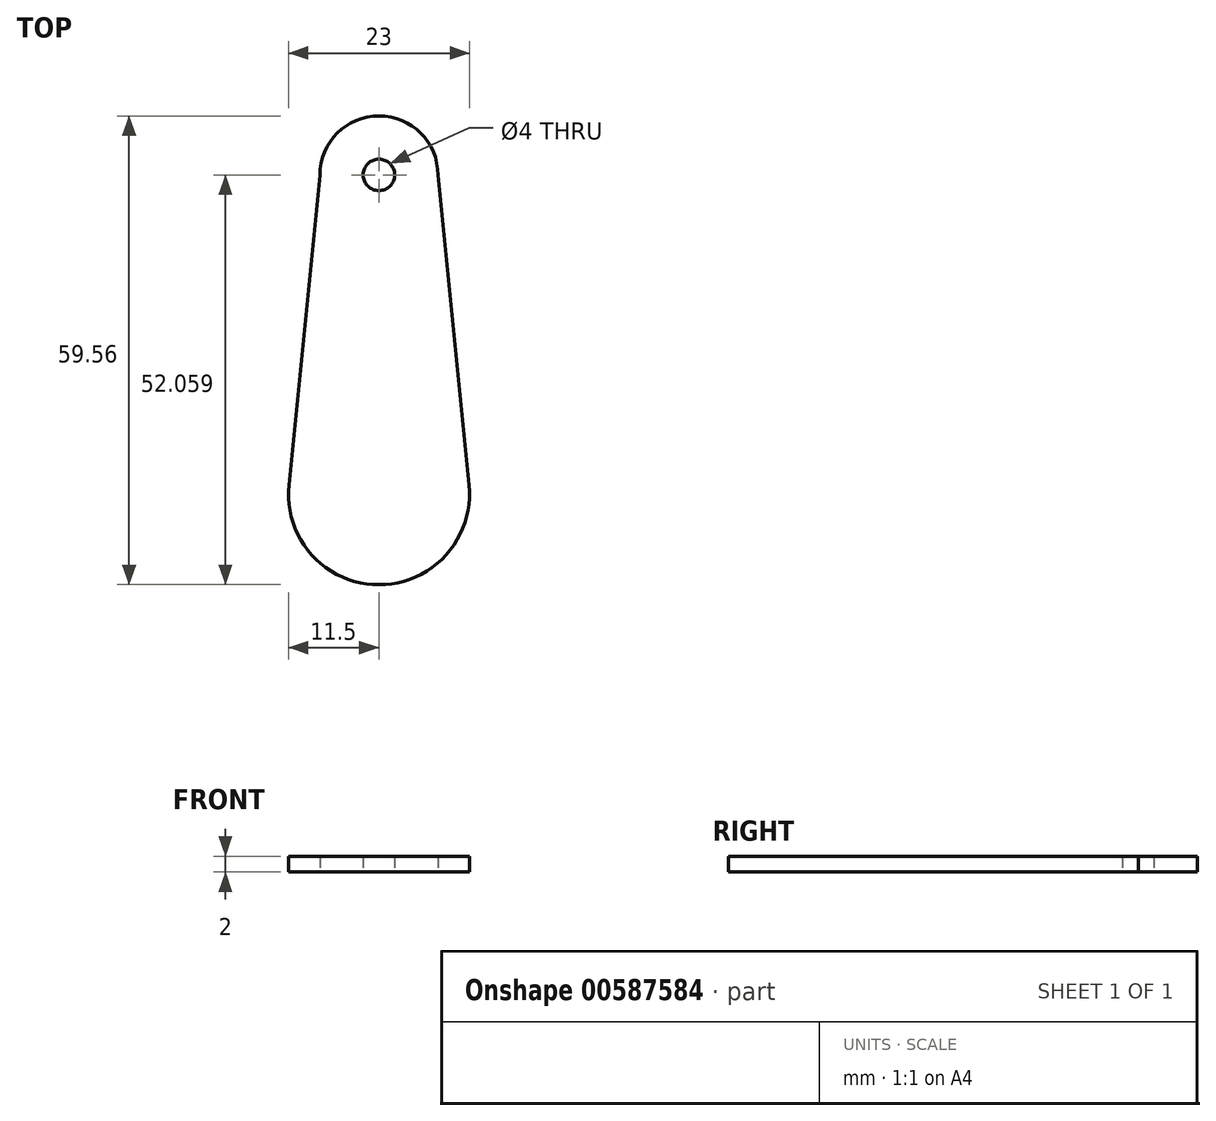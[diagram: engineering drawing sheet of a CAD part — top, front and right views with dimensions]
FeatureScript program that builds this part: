
annotation { "Feature Type Name" : "Feature", "Feature Type Description" : "" }
export const myFeature = defineFeature(function(context is Context, id is Id, definition is map)
    precondition{}
    {
        {
            var Q0;
            Q0=qCreatedBy(makeId("Top.planeOp"),FACE);
            var sketch = newSketch(context, id + "F0", { "sketchPlane" : qUnion([Q0])});
            skArc(sketch, "E0", {"start": v(-11.44, 1.14) * mm, "mid": v(0, -11.5) * mm, "end": v(11.44, 1.14) * mm});
            skArc(sketch, "E1", {"start": v(7.5, 40.56) * mm, "mid": v(0, 48.06) * mm, "end": v(-7.5, 40.56) * mm});
            skLineSegment(sketch, "E2", {"start": v(-7.5, 40.56) * mm, "end": v(-11.56, 0) * mm});
            skLineSegment(sketch, "E3", {"start": v(7.5, 40.56) * mm, "end": v(11.56, 0) * mm});
            skCircle(sketch, "E4", {"center": v(0, 40.56) * mm, "radius": 2 * mm});
            skSolve(sketch);
        }
        {
            var Q0;
            Q0 = qSketchRegion(id + "F0", true);
            extrude(context, id + "F1", {"entities" : qUnion([Q0]), "depth" : 2 * mm, "offsetDistance" : 25 * mm});
        }
    });
